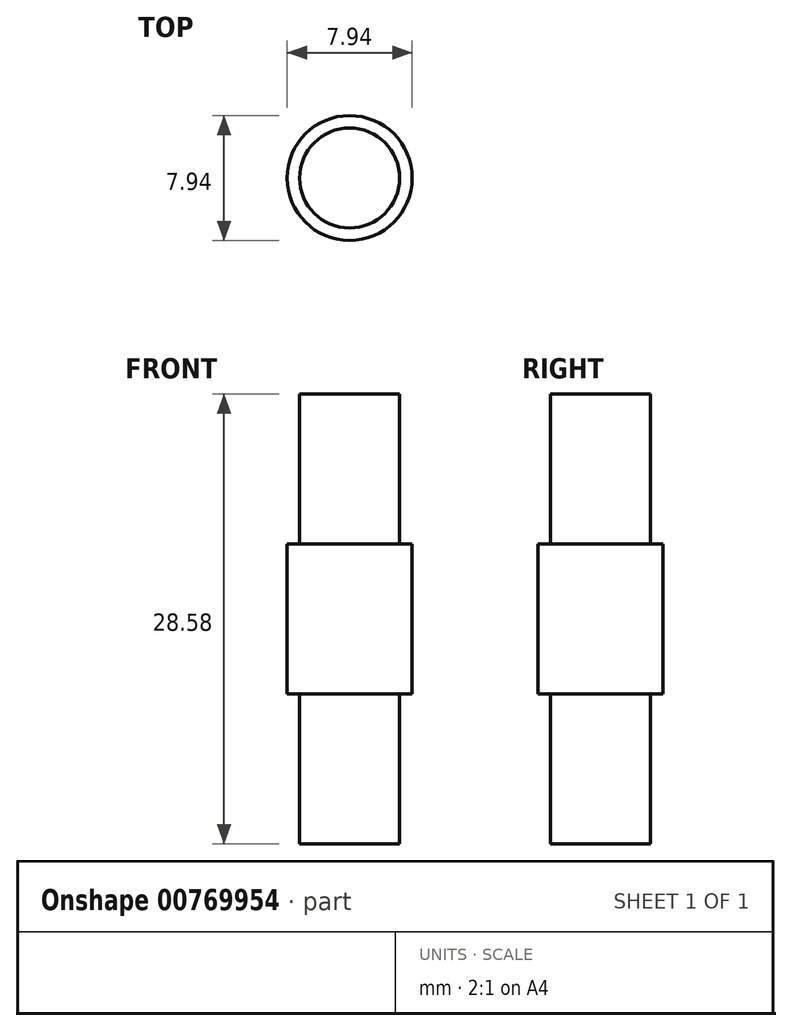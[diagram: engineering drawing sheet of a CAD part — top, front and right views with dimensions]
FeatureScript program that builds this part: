
annotation { "Feature Type Name" : "Feature", "Feature Type Description" : "" }
export const myFeature = defineFeature(function(context is Context, id is Id, definition is map)
    precondition{}
    {
        {
            var Q0;
            Q0=qCreatedBy(makeId("Front.planeOp"),FACE);
            var sketch = newSketch(context, id + "F0", { "sketchPlane" : qUnion([Q0])});
            skLineSegment(sketch, "E0", {"start": v(0, 14.29) * mm, "end": v(-3.17, 14.29) * mm});
            skLineSegment(sketch, "E1", {"start": v(-3.18, 14.29) * mm, "end": v(-3.18, 4.76) * mm});
            skLineSegment(sketch, "E2", {"start": v(-3.18, 4.76) * mm, "end": v(-3.97, 4.76) * mm});
            skLineSegment(sketch, "E3", {"start": v(-3.97, 4.76) * mm, "end": v(-3.97, -4.76) * mm});
            skLineSegment(sketch, "E4", {"start": v(-3.97, -4.76) * mm, "end": v(-3.18, -4.76) * mm});
            skLineSegment(sketch, "E5", {"start": v(-3.18, -4.76) * mm, "end": v(-3.17, -14.29) * mm});
            skLineSegment(sketch, "E6", {"start": v(-3.17, -14.29) * mm, "end": v(0, -14.29) * mm});
            skLineSegment(sketch, "E7", {"start": v(0, -14.29) * mm, "end": v(0, 14.29) * mm});
            skSolve(sketch);
        }
        {
            var Q0;
            Q0=makeQuery(id+"F0.imprint","IMPRINT",FACE,{"disambiguationData":[TD([[makeQuery(id+"F0.imprint","IMPRINT",EDGE,{"derivedFrom":sQuery(id+"F0.wireOp",EDGE,"E0")}),1.0]])]});
            var Q1;
            Q1=sQuery(id+"F0.wireOp",EDGE,"E7");
            revolve(context, id + "F1", {"surfaceOperationType" : NewSurfaceOperationType.NEW, "entities" : qUnion([Q0]), "axis" : qUnion([Q1]), "revolveType" : RevolveType.FULL});
        }
    });
